# Revit family: Mantel_NativeCustomStone
name_source: partatom
category: Generic Models
revit_build: Autodesk Revit 2013 (Build: 20120221_2030(x64)
units: mm (PartAtom-declared; Revit-internal decimal feet)

## types (1)
- Mantel_NativeCustomStone
    Assembly Code = B2010100
    Construction Details = http://www.nativecustomstone.com
    Default Elevation = 0' - 0"
    Description = Mantel as Specified in 04 73 00
    Green Building-LEED = http://www.nativecustomstone.com
    Installation Phase = Masonry Finishes
    Installation-Fabrication = http://www.nativecustomstone.com
    Keynote = 04 73 00
    Maintenance Schedule (Months) = 12
    Manufacturer = Native Custom Stone
    Manufacturer Fax = 706-216-5550
    Manufacturer Website = www.nativecstone.com
    Material = Native-Custom-Stone_Accessory-Material_Buff-Color
    Model = As Specified in 04 73 00
    Product Data = http://www.arcat.com
    Product Properties = http://www.nativecustomstone.com
    Revision = R1_10-2012
    Sales Information = http://www.nativecustomstone.com
    Send Message = http://www.arcat.com
    Specification = http://www.nativecustomstone.com
    Test Data = http://www.nativecustomstone.com
    URL = http://www.nativecustomstone.com
    Unit Width = 5' - 0"
    Warranty Duration (Years) = 50

## geometry (parser evidence)
native form markers: Blend x14, Sweep x1
no freeform markers — native parametric forms only
